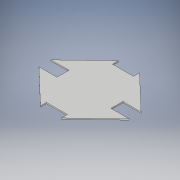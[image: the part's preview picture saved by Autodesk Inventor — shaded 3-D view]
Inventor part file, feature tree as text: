
AUTODESK INVENTOR PART (.ipt)
format: ipt  version: 2018 (Build 220112000, 112)  size: 117,248 bytes
history: native  units: in
note: dims shown in document units (in); Inventor stores cm internally (conversion verified against a paired STEP export)
features: extrude x1, sketch x1
ambient origin geometry x8: Origin, YZ Plane, XZ Plane, XY Plane, X Axis, Y Axis, Z Axis, Center Point
bodies: Body1 (feature_tree)
feature tree (2):
  extrude  "Wood Base"  Depth=4.0in
  sketch  "Sketch1"  dims[d9=6.0in d10=4.0in d14=6.0in d15=4.0in d24=0.375in d25=0.0in d27=7.0in d29=7.0in d30=2.0in d31=2.0in d32=2.0in]
